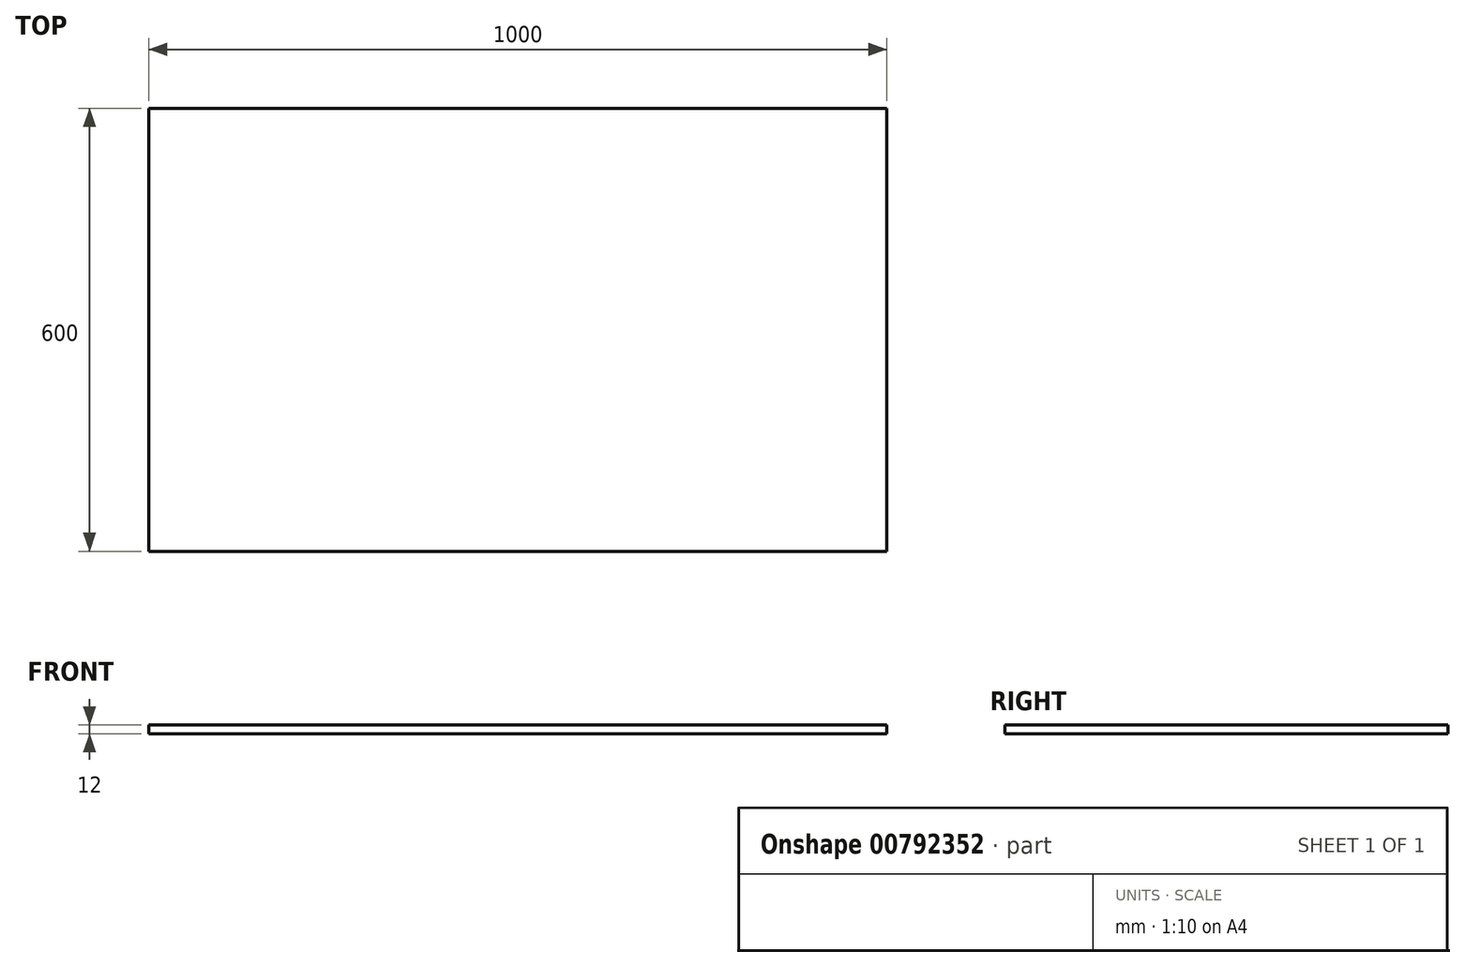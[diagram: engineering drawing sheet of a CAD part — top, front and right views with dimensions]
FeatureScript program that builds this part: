
annotation { "Feature Type Name" : "Feature", "Feature Type Description" : "" }
export const myFeature = defineFeature(function(context is Context, id is Id, definition is map)
    precondition{}
    {
        {
            var Q0;
            Q0=qCreatedBy(makeId("Top.planeOp"),FACE);
            var sketch = newSketch(context, id + "F0", { "sketchPlane" : qUnion([Q0])});
            skLineSegment(sketch, "E0.bottom", {"start": v(-500, 300) * mm, "end": v(500, 300) * mm});
            skLineSegment(sketch, "E0.top", {"start": v(-500, -300) * mm, "end": v(500, -300) * mm});
            skLineSegment(sketch, "E0.left", {"start": v(-500, 300) * mm, "end": v(-500, -300) * mm});
            skLineSegment(sketch, "E0.right", {"start": v(500, 300) * mm, "end": v(500, -300) * mm});
            skPoint(sketch, "E0.middle", {"position": v(0, 0) * mm});
            skSolve(sketch);
        }
        {
            var Q0;
            Q0=makeQuery(id+"F0.imprint","IMPRINT",FACE,{"disambiguationData":[TD([[makeQuery(id+"F0.imprint","IMPRINT",EDGE,{"derivedFrom":sQuery(id+"F0.wireOp",EDGE,"E0.bottom")}),-1.0]])]});
            extrude(context, id + "F1", {"entities" : qUnion([Q0]), "depth" : 12 * mm, "offsetDistance" : 25 * mm});
        }
    });
